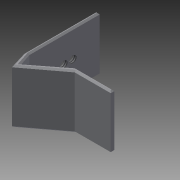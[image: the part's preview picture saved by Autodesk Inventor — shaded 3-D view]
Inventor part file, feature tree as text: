
AUTODESK INVENTOR PART (.ipt)
format: ipt  version: 2015 (Build 190159000, 159)  size: 121,344 bytes
history: native  units: in
note: dims shown in document units (in); Inventor stores cm internally (conversion verified against a paired STEP export)
features: sketch x2, extrude x1, hole x1, chamfer x1
ambient origin geometry x8: Origin, YZ Plane, XZ Plane, XY Plane, X Axis, Y Axis, Z Axis, Center Point
bodies: Solid1 (feature_tree)
feature tree (5):
  extrude  "Extrusion1"  Depth=1.0in
  hole  "Hole1"  [1 undecoded]
  chamfer  "Chamfer1"  Distance=0.481in
  sketch  "Sketch1"  dims[d0=0.75in d1=1.0in]
  sketch  "Sketch2"  dims[d2=2.0in d3=0.481in d4=0.481in d5=0.1in d6=0.1in d7=1.0in d8=1.5in d9=0.0in d10=0.75in d11=0.25in d12=0.75in d13=0.196in d14=0.5in d15=0.375in d16=0.25in d17=0.5635in d18=1.0in d19=0.8108in d20=0.04in d21=0.125in d22=45.0deg]
note: 1 required parameter value undecoded (feature->parameter linkage not recoverable at this tier; creation-order binding heuristic only, values carry confidence <= 0.55)
